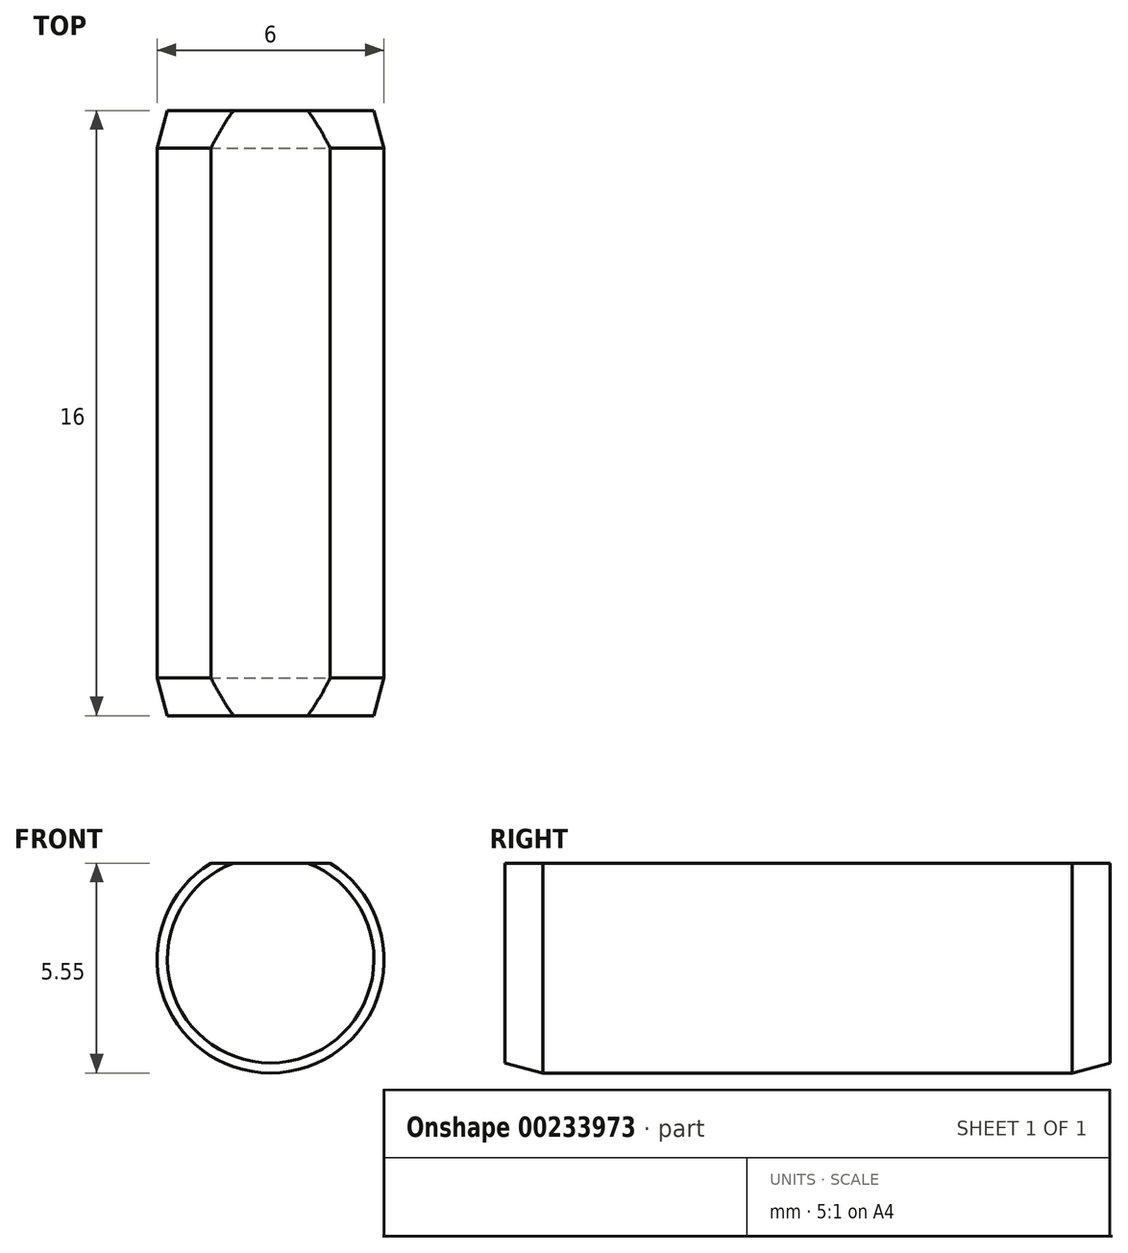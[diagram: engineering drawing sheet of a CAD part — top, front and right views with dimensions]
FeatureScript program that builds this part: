
annotation { "Feature Type Name" : "Feature", "Feature Type Description" : "" }
export const myFeature = defineFeature(function(context is Context, id is Id, definition is map)
    precondition{}
    {
        {
            assignVariable(context, id + "F0", {"variableType" : VariableType.LENGTH, "name" : "L", "lengthValue" : 16 * mm});
        }
        {
            var Q0;
            Q0=qCreatedBy(makeId("Front.planeOp"),FACE);
            var sketch = newSketch(context, id + "F1", { "sketchPlane" : qUnion([Q0])});
            skCircle(sketch, "E0", {"center": v(0, 0) * mm, "radius": 3 * mm});
            skSolve(sketch);
        }
        {
            var Q0;
            Q0=makeQuery(id+"F1.imprint","IMPRINT",FACE,{"disambiguationData":[TD([[makeQuery(id+"F1.imprint","IMPRINT",EDGE,{"derivedFrom":sQuery(id+"F1.wireOp",EDGE,"E0")}),1.0]])]});
            extrude(context, id + "F2", {"entities" : qUnion([Q0]), "endBound" : BoundingType.SYMMETRIC, "depth" : getVariable(context, 'L'), "offsetDistance" : 25 * mm});
        }
        {
            var Q0;
            Q0=makeQuery(id+"F2.opExtrude","CAP_EDGE",EDGE,{"disambiguationData":[OSD([sQuery(id+"F1.wireOp",EDGE,"E0")])],"isStart":false});
            var Q1;
            Q1=makeQuery(id+"F2.opExtrude","CAP_EDGE",EDGE,{"disambiguationData":[OSD([sQuery(id+"F1.wireOp",EDGE,"E0")])],"isStart":true});
            chamfer(context, id + "F3", {"entities" : qUnion([Q0, Q1]), "chamferType" : ChamferType.OFFSET_ANGLE, "width" : 1 * mm, "oppositeDirection" : true, "angle" : 15 * degree, "tangentPropagation" : true});
        }
        {
            var Q0;
            Q0=qCreatedBy(makeId("Front.planeOp"),FACE);
            var sketch = newSketch(context, id + "F4", { "sketchPlane" : qUnion([Q0])});
            skLineSegment(sketch, "E1", {"start": v(-3, 2.55) * mm, "end": v(3, 2.55) * mm});
            skLineSegment(sketch, "E2", {"start": v(-3, 2.55) * mm, "end": v(-3, 8.55) * mm});
            skLineSegment(sketch, "E3", {"start": v(-3, 8.55) * mm, "end": v(3, 8.55) * mm});
            skLineSegment(sketch, "E4", {"start": v(3, 8.55) * mm, "end": v(3, 2.55) * mm});
            skPoint(sketch, "E5", {"position": v(0, 2.55) * mm});
            skSolve(sketch);
        }
        {
            var Q0;
            Q0=makeQuery(id+"F4.imprint","IMPRINT",FACE,{"disambiguationData":[TD([[makeQuery(id+"F4.imprint","IMPRINT",EDGE,{"derivedFrom":sQuery(id+"F4.wireOp",EDGE,"E1")}),1.0]])]});
            extrude(context, id + "F5", {"entities" : qUnion([Q0]), "operationType" : NewBodyOperationType.REMOVE, "endBound" : BoundingType.SYMMETRIC, "oppositeDirection" : true, "depth" : getVariable(context, 'L'), "offsetDistance" : 25 * mm});
        }
    });
